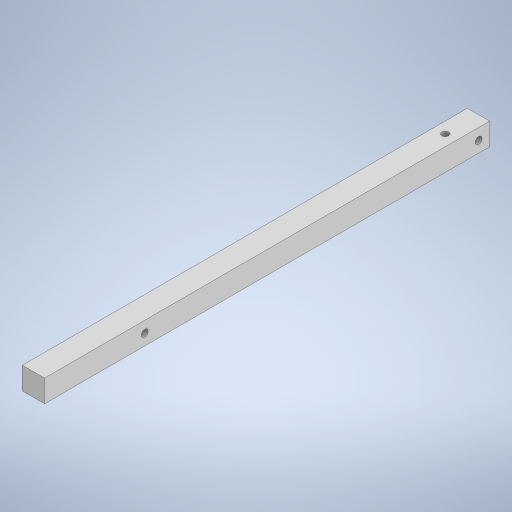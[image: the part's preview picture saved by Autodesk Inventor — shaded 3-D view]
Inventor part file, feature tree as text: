
AUTODESK INVENTOR PART (.ipt)
format: ipt  version: 2023 (Build 270158000, 158)  size: 243,200 bytes
history: native  units: mm
features: sketch x3, hole x2, other x1, extrude x1
ambient origin geometry x8: Origin, YZ Plane, XZ Plane, XY Plane, X Axis, Y Axis, Z Axis, Center Point
bodies: Body1 (feature_tree)
feature tree (7):
  other  "ソリッド1"
  extrude  "押し出し1"  Depth=10.0mm
  hole  "穴1"  [1 undecoded]
  hole  "穴2"  [1 undecoded]
  sketch  "スケッチ1"
  sketch  "スケッチ2"
  sketch  "スケッチ3"
note: 2 required parameter values undecoded (feature->parameter linkage not recoverable at this tier; creation-order binding heuristic only, values carry confidence <= 0.55)
